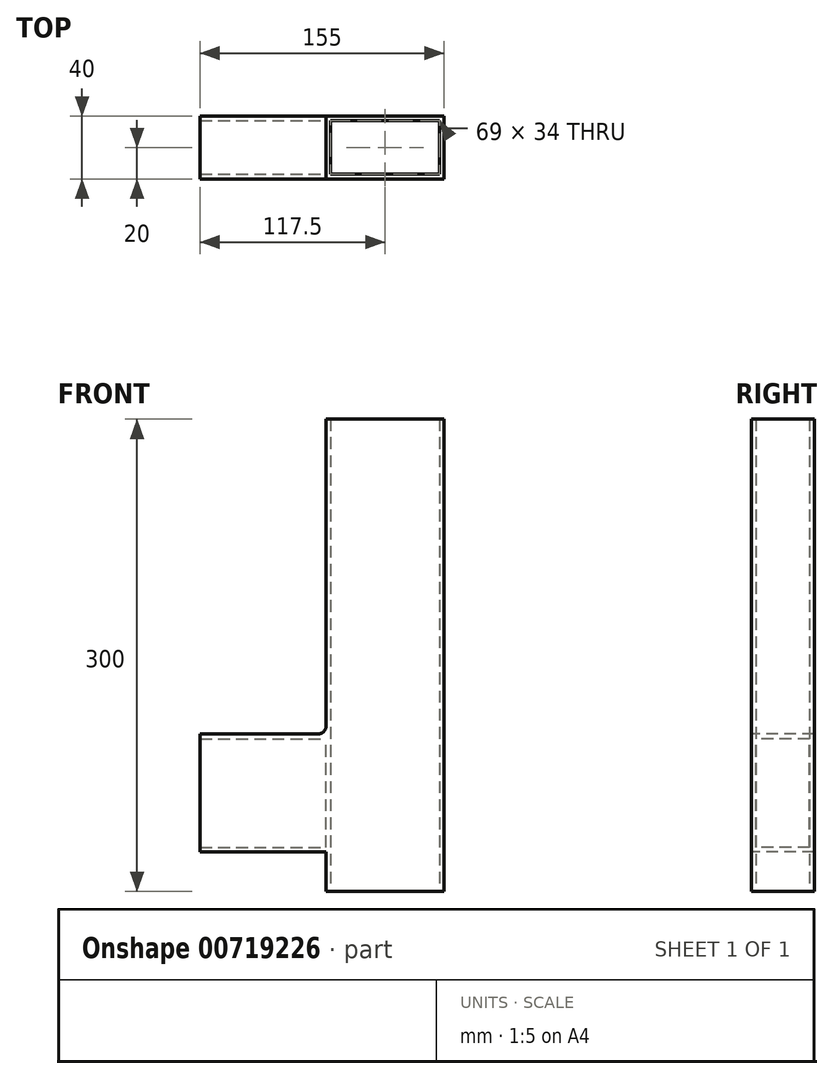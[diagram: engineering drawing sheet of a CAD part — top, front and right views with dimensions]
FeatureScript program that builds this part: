
annotation { "Feature Type Name" : "Feature", "Feature Type Description" : "" }
export const myFeature = defineFeature(function(context is Context, id is Id, definition is map)
    precondition{}
    {
        {
            var Q0;
            Q0=qCreatedBy(makeId("Top.planeOp"),FACE);
            var sketch = newSketch(context, id + "F0", { "sketchPlane" : qUnion([Q0])});
            skLineSegment(sketch, "E0.bottom", {"start": v(0, 0) * mm, "end": v(-75, 0) * mm});
            skLineSegment(sketch, "E0.top", {"start": v(0, 40) * mm, "end": v(-75, 40) * mm});
            skLineSegment(sketch, "E0.left", {"start": v(0, 0) * mm, "end": v(0, 40) * mm});
            skLineSegment(sketch, "E0.right", {"start": v(-75, 0) * mm, "end": v(-75, 40) * mm});
            skLineSegment(sketch, "E1.0", {"start": v(-3, 3) * mm, "end": v(-72, 3) * mm});
            skLineSegment(sketch, "E1.1", {"start": v(-3, 3) * mm, "end": v(-3, 37) * mm});
            skLineSegment(sketch, "E1.2", {"start": v(-3, 37) * mm, "end": v(-72, 37) * mm});
            skLineSegment(sketch, "E1.3", {"start": v(-72, 3) * mm, "end": v(-72, 37) * mm});
            skSolve(sketch);
        }
        {
            var Q0;
            Q0 = qSketchRegion(id + "F0", true);
            extrude(context, id + "F1", {"entities" : qUnion([Q0]), "depth" : 300 * mm, "offsetDistance" : 25 * mm});
        }
        {
            var Q0;
            Q0=makeQuery(id+"F1.opExtrude","SWEPT_FACE",FACE,{"disambiguationData":[OSD([sQuery(id+"F0.wireOp",EDGE,"E0.right")])]});
            var sketch = newSketch(context, id + "F2", { "sketchPlane" : qUnion([Q0])});
            skLineSegment(sketch, "E2.bottom", {"start": v(-40, 25) * mm, "end": v(0, 25) * mm});
            skLineSegment(sketch, "E2.top", {"start": v(-40, 100) * mm, "end": v(0, 100) * mm});
            skLineSegment(sketch, "E2.left", {"start": v(-40, 25) * mm, "end": v(-40, 100) * mm});
            skLineSegment(sketch, "E2.right", {"start": v(0, 25) * mm, "end": v(0, 100) * mm});
            skLineSegment(sketch, "E3.0", {"start": v(-37, 97) * mm, "end": v(-3, 97) * mm});
            skLineSegment(sketch, "E3.1", {"start": v(-37, 28) * mm, "end": v(-37, 97) * mm});
            skLineSegment(sketch, "E3.2", {"start": v(-37, 28) * mm, "end": v(-3, 28) * mm});
            skLineSegment(sketch, "E3.3", {"start": v(-3, 28) * mm, "end": v(-3, 97) * mm});
            skSolve(sketch);
        }
        {
            var Q0;
            Q0 = qSketchRegion(id + "F2", true);
            extrude(context, id + "F3", {"entities" : qUnion([Q0]), "operationType" : NewBodyOperationType.ADD, "depth" : 80 * mm, "offsetDistance" : 25 * mm});
        }
        {
            var Q0;
            Q0=makeQuery(id+"F3.opExtrude","CAP_EDGE",EDGE,{"disambiguationData":[OSD([sQuery(id+"F2.wireOp",EDGE,"E2.top")])],"isStart":true});
            var Q1;
            Q1=makeQuery(id+"F3.opExtrude","CAP_EDGE",EDGE,{"disambiguationData":[OSD([sQuery(id+"F2.wireOp",EDGE,"E2.bottom")])],"isStart":true});
            fillet(context, id + "F4", {"entities" : qUnion([Q0, Q1]), "radius" : 5 * mm, "tangentPropagation" : true, "allowEdgeOverflow" : false});
        }
    });
